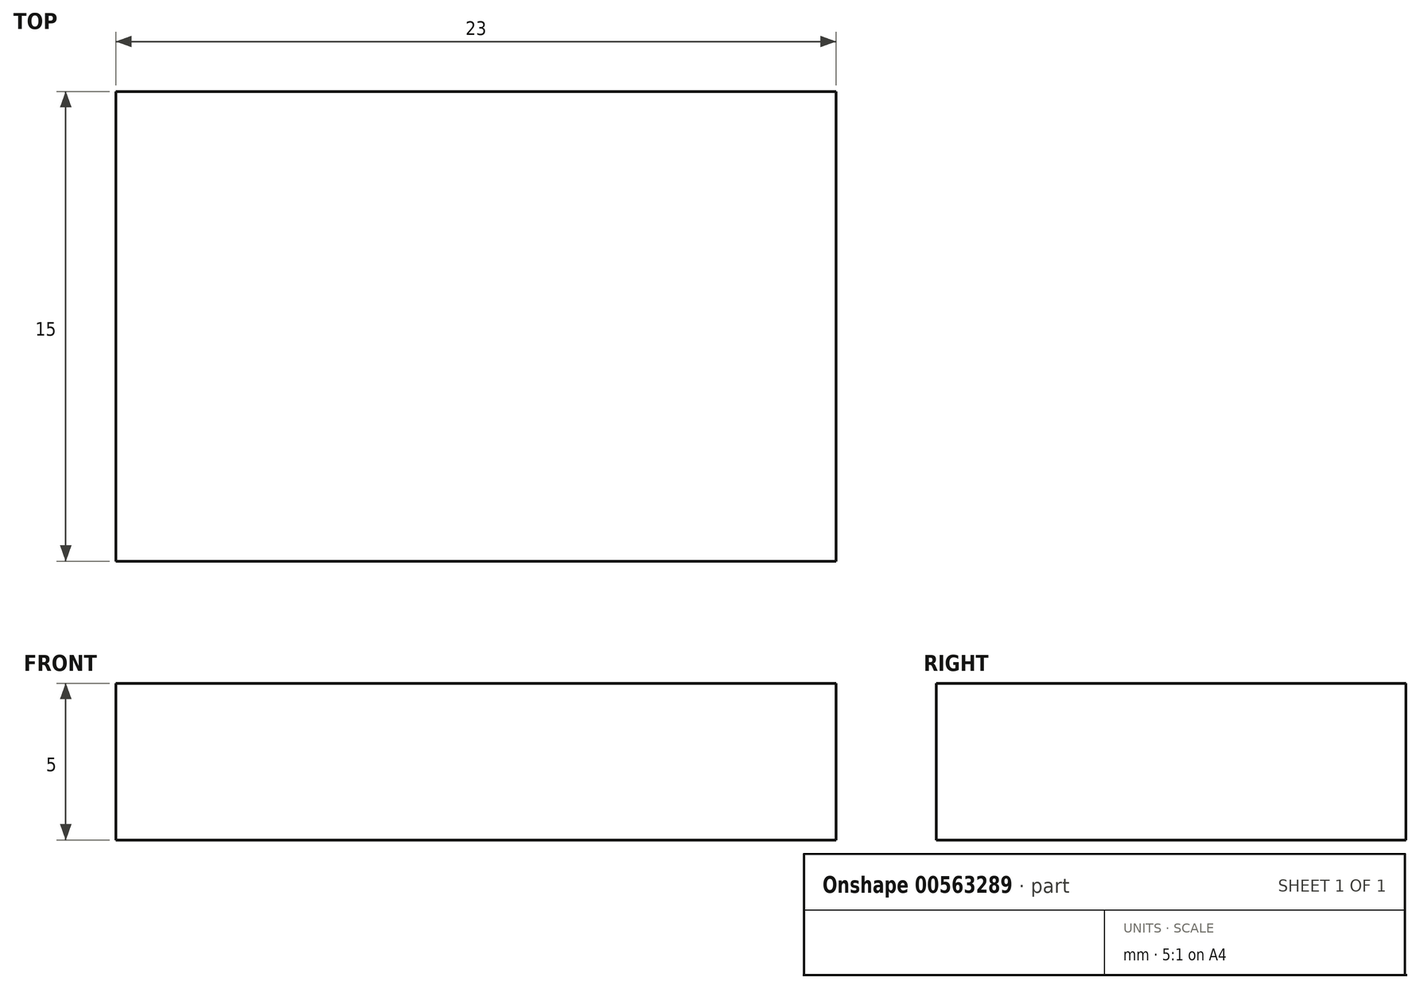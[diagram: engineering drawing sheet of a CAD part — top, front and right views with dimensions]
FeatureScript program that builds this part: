
annotation { "Feature Type Name" : "Feature", "Feature Type Description" : "" }
export const myFeature = defineFeature(function(context is Context, id is Id, definition is map)
    precondition{}
    {
        {
            var Q0;
            Q0=qCreatedBy(makeId("Top.planeOp"),FACE);
            var sketch = newSketch(context, id + "F0", { "sketchPlane" : qUnion([Q0])});
            skLineSegment(sketch, "E0.bottom", {"start": v(0, 0) * mm, "end": v(-23, 0) * mm});
            skLineSegment(sketch, "E0.top", {"start": v(0, 15) * mm, "end": v(-23, 15) * mm});
            skLineSegment(sketch, "E0.left", {"start": v(0, 0) * mm, "end": v(0, 15) * mm});
            skLineSegment(sketch, "E0.right", {"start": v(-23, 0) * mm, "end": v(-23, 15) * mm});
            skSolve(sketch);
        }
        {
            var Q0;
            Q0 = qSketchRegion(id + "F0", true);
            extrude(context, id + "F1", {"entities" : qUnion([Q0]), "depth" : 5 * mm, "offsetDistance" : 25 * mm});
        }
    });
